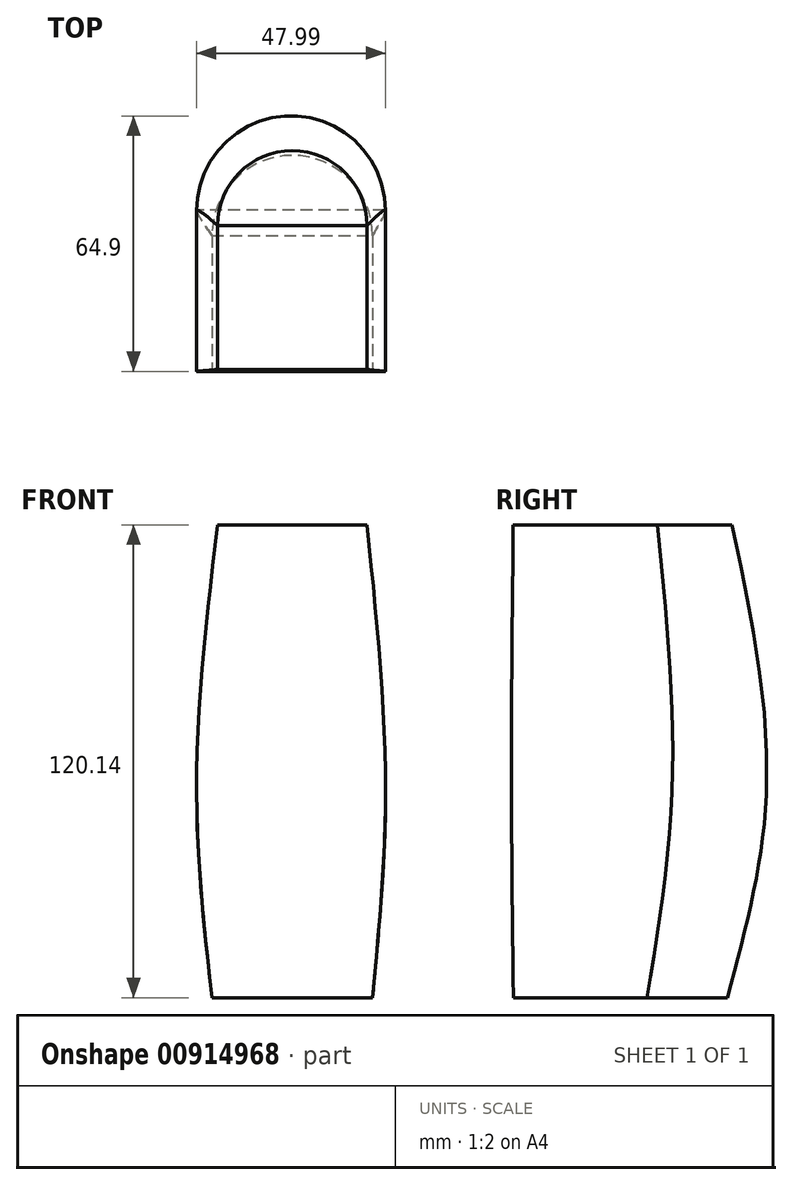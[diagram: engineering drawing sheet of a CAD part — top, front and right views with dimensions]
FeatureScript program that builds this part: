
annotation { "Feature Type Name" : "Feature", "Feature Type Description" : "" }
export const myFeature = defineFeature(function(context is Context, id is Id, definition is map)
    precondition{}
    {
        {
            var Q0;
            Q0=qCreatedBy(makeId("Top.planeOp"),FACE);
            var sketch = newSketch(context, id + "F0", { "sketchPlane" : qUnion([Q0])});
            skLineSegment(sketch, "E0.bottom", {"start": v(-31.94, 19.42) * mm, "end": v(8.86, 19.42) * mm});
            skLineSegment(sketch, "E0.top", {"start": v(-31.94, -14.57) * mm, "end": v(8.86, -14.57) * mm});
            skLineSegment(sketch, "E0.left", {"start": v(-31.94, 19.42) * mm, "end": v(-31.94, -14.57) * mm});
            skLineSegment(sketch, "E0.right", {"start": v(8.86, 19.42) * mm, "end": v(8.86, -14.57) * mm});
            skArc(sketch, "E1", {"start": v(8.86, 19.42) * mm, "mid": v(-11.54, 39.82) * mm, "end": v(-31.94, 19.42) * mm});
            skSolve(sketch);
        }
        {
            var Q0;
            Q0=makeQuery(id+"F0.imprint","IMPRINT",FACE,{"disambiguationData":[TD([[makeQuery(id+"F0.imprint","IMPRINT",EDGE,{"derivedFrom":sQuery(id+"F0.wireOp",EDGE,"E0.bottom")}),-1.0]])]});
            cPlane(context, id + "F1", {"entities" : qUnion([Q0]), "cplaneType" : CPlaneType.OFFSET, "offset" : 47.24 * mm, "width" : 152.4 * mm, "height" : 152.4 * mm});
        }
        {
            var Q0;
            Q0=qCreatedBy(id+"F1.planeOp",FACE);
            var sketch = newSketch(context, id + "F2", { "sketchPlane" : qUnion([Q0])});
            skLineSegment(sketch, "E2.bottom", {"start": v(-35.79, -15.03) * mm, "end": v(12.1, -15.03) * mm});
            skLineSegment(sketch, "E2.top", {"start": v(-35.79, 25.52) * mm, "end": v(12.1, 25.52) * mm});
            skLineSegment(sketch, "E2.left", {"start": v(-35.79, -15.03) * mm, "end": v(-35.79, 25.52) * mm});
            skLineSegment(sketch, "E2.right", {"start": v(12.1, -15.03) * mm, "end": v(12.1, 25.52) * mm});
            skArc(sketch, "E3", {"start": v(12.1, 25.52) * mm, "mid": v(-11.85, 49.46) * mm, "end": v(-35.79, 25.52) * mm});
            skSolve(sketch);
        }
        {
            var Q0;
            Q0=makeQuery(id+"F2.imprint","IMPRINT",FACE,{"disambiguationData":[TD([[makeQuery(id+"F2.imprint","IMPRINT",EDGE,{"derivedFrom":sQuery(id+"F2.wireOp",EDGE,"E2.bottom")}),1.0]])]});
            cPlane(context, id + "F3", {"entities" : qUnion([Q0]), "cplaneType" : CPlaneType.OFFSET, "offset" : 72.9 * mm, "width" : 152.4 * mm, "height" : 152.4 * mm});
        }
        {
            var Q0;
            Q0=qCreatedBy(id+"F3.planeOp",FACE);
            var sketch = newSketch(context, id + "F4", { "sketchPlane" : qUnion([Q0])});
            skLineSegment(sketch, "E4.bottom", {"start": v(-30.52, 22.02) * mm, "end": v(7.44, 22.02) * mm});
            skLineSegment(sketch, "E4.top", {"start": v(-30.52, -14.6) * mm, "end": v(7.44, -14.6) * mm});
            skLineSegment(sketch, "E4.left", {"start": v(-30.52, 22.02) * mm, "end": v(-30.52, -14.6) * mm});
            skLineSegment(sketch, "E4.right", {"start": v(7.44, 22.02) * mm, "end": v(7.44, -14.6) * mm});
            skArc(sketch, "E5", {"start": v(7.44, 22.02) * mm, "mid": v(-11.54, 41) * mm, "end": v(-30.52, 22.02) * mm});
            skSolve(sketch);
        }
        {
            var Q0;
            Q0=makeQuery(id+"F0.imprint","IMPRINT",FACE,{"disambiguationData":[TD([[makeQuery(id+"F0.imprint","IMPRINT",EDGE,{"derivedFrom":sQuery(id+"F0.wireOp",EDGE,"E0.bottom")}),-1.0]])]});
            var Q1;
            Q1=makeQuery(id+"F2.imprint","IMPRINT",FACE,{"disambiguationData":[TD([[makeQuery(id+"F2.imprint","IMPRINT",EDGE,{"derivedFrom":sQuery(id+"F2.wireOp",EDGE,"E2.bottom")}),1.0]])]});
            var Q2;
            Q2=makeQuery(id+"F4.imprint","IMPRINT",FACE,{"disambiguationData":[TD([[makeQuery(id+"F4.imprint","IMPRINT",EDGE,{"derivedFrom":sQuery(id+"F4.wireOp",EDGE,"E4.bottom")}),-1.0]])]});
            loft(context, id + "F5", {"sheetProfilesArray" : [{ "sheetProfileEntities" : qUnion([Q0]) }, { "sheetProfileEntities" : qUnion([Q1]) }, { "sheetProfileEntities" : qUnion([Q2]) }]});
        }
        {
            var Q1;
            Q1=makeQuery(id+"F4.imprint","IMPRINT",FACE,{"disambiguationData":[TD([[makeQuery(id+"F4.imprint","IMPRINT",EDGE,{"derivedFrom":sQuery(id+"F4.wireOp",EDGE,"E4.bottom")}),1.0]])]});
            var Q2;
            Q2=makeQuery(id+"F2.imprint","IMPRINT",FACE,{"disambiguationData":[TD([[makeQuery(id+"F2.imprint","IMPRINT",EDGE,{"derivedFrom":sQuery(id+"F2.wireOp",EDGE,"E2.top")}),1.0]])]});
            var Q3;
            Q3=makeQuery(id+"F0.imprint","IMPRINT",FACE,{"disambiguationData":[TD([[makeQuery(id+"F0.imprint","IMPRINT",EDGE,{"derivedFrom":sQuery(id+"F0.wireOp",EDGE,"E0.bottom")}),1.0]])]});
            loft(context, id + "F6", {"sheetProfilesArray" : [{ "sheetProfileEntities" : qUnion([Q1]) }, { "sheetProfileEntities" : qUnion([Q2]) }, { "sheetProfileEntities" : qUnion([Q3]) }]});
        }
    });
